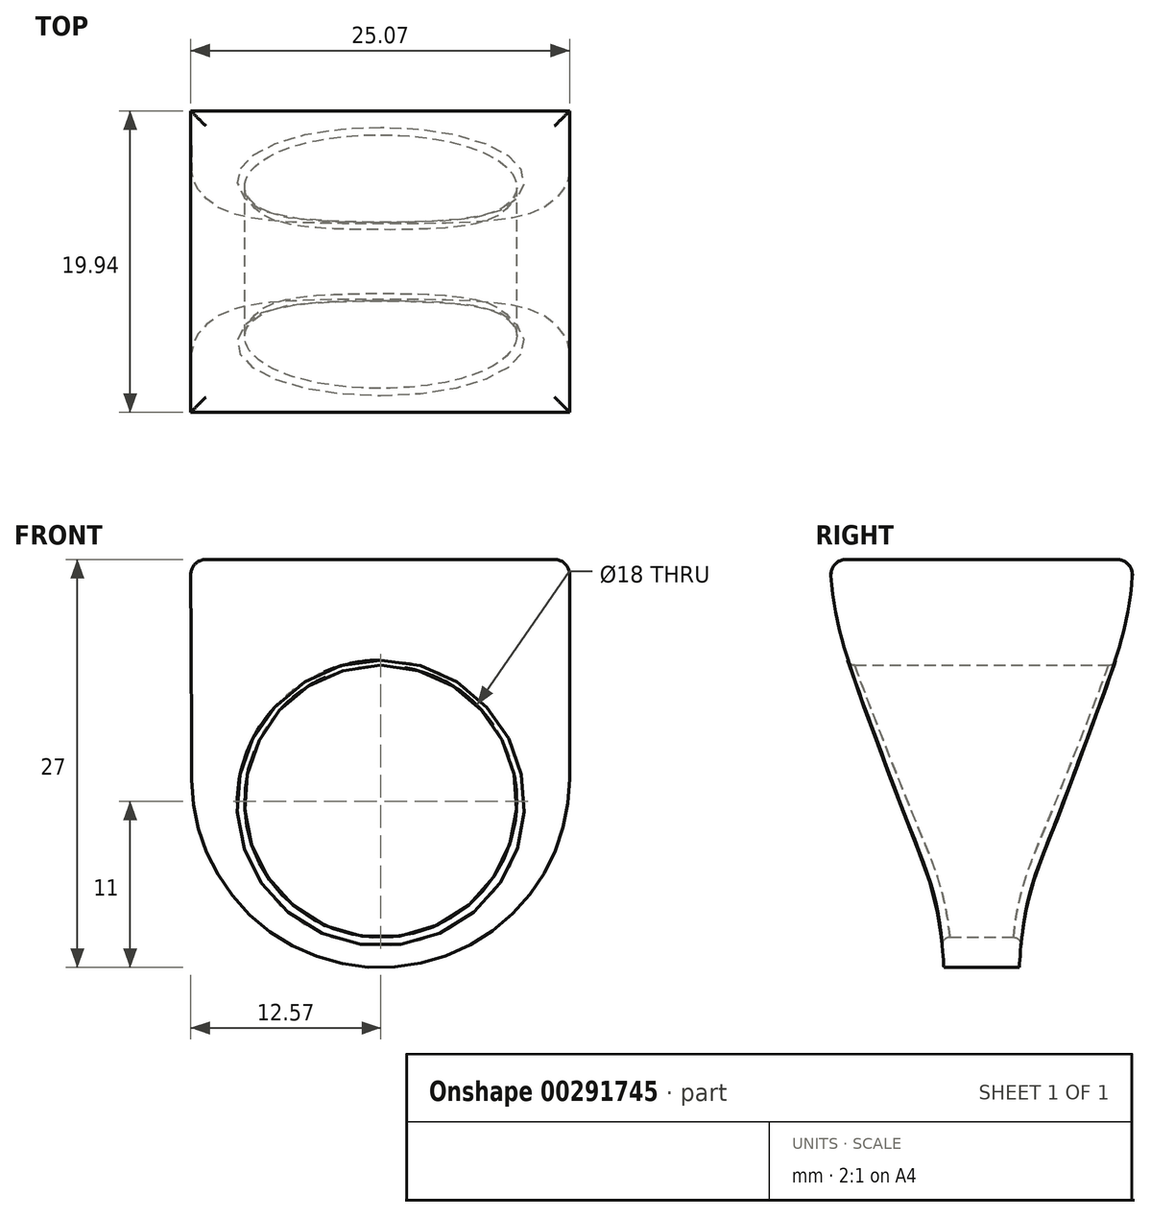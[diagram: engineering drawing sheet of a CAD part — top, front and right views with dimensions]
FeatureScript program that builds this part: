
annotation { "Feature Type Name" : "Feature", "Feature Type Description" : "" }
export const myFeature = defineFeature(function(context is Context, id is Id, definition is map)
    precondition{}
    {
        {
            assignVariable(context, id + "F0", {"name" : "ring_brete", "anyValue" : 20 * mm});
        }
        {
            var Q0;
            Q0=qCreatedBy(makeId("Front.planeOp"),FACE);
            var sketch = newSketch(context, id + "F1", { "sketchPlane" : qUnion([Q0])});
            skCircle(sketch, "E0", {"center": v(0, 0) * mm, "radius": 9 * mm});
            skCircle(sketch, "E1", {"center": v(0, 1.5) * mm, "radius": 12.5 * mm});
            skLineSegment(sketch, "E2", {"start": v(-12.5, 1.43) * mm, "end": v(-12.58, 16) * mm});
            skLineSegment(sketch, "E3", {"start": v(-12.58, 16) * mm, "end": v(12.5, 16) * mm});
            skLineSegment(sketch, "E4", {"start": v(12.5, 16) * mm, "end": v(12.5, 1.5) * mm});
            skSolve(sketch);
        }
        {
            var Q0;
            {var subQ0=sQuery(id+"F1.wireOp",EDGE,"E2");Q0=makeQuery(id+"F1.imprint","IMPRINT",FACE,{"disambiguationData":[TD([[makeQuery(id+"F1.imprint","IMPRINT",EDGE,{"derivedFrom":subQ0}),-1.0]])]});}
            var Q1;
            Q1=makeQuery(id+"F1.imprint","IMPRINT",FACE,{"disambiguationData":[TD([[makeQuery(id+"F1.imprint","IMPRINT",EDGE,{"derivedFrom":sQuery(id+"F1.wireOp",EDGE,"E0")}),-1.0]])]});
            extrude(context, id + "F2", {"entities" : qUnion([Q0, Q1]), "depth" : getVariable(context, 'ring_brete'), "offsetDistance" : 25 * mm, "symmetric" : true});
        }
        {
            var Q0;
            Q0=makeQuery(id+"F2.opExtrude","SWEPT_FACE",FACE,{"disambiguationData":[OSD([sQuery(id+"F1.wireOp",EDGE,"E2")])]});
            var sketch = newSketch(context, id + "F3", { "sketchPlane" : qUnion([Q0])});
            skLineSegment(sketch, "E5.0", {"start": v(10, 16.07) * mm, "end": v(-10, 16.07) * mm, "construction": true});
            skLineSegment(sketch, "E6", {"start": v(10, -11) * mm, "end": v(-10, -11) * mm, "construction": true});
            skLineSegment(sketch, "E7.0", {"start": v(10, 1.5) * mm, "end": v(10, 16.07) * mm, "construction": true});
            skFitSpline(sketch, "E8", {"points": [v(10, 16.07) * mm, v(8, 6.88) * mm, v(4.5, -2.44) * mm, v(2.5, -11) * mm], "startDerivative": vector(0, -32.36) * mm, "endDerivative": vector(-1.97, -39.16) * mm});
            skLineSegment(sketch, "E9", {"start": v(2.5, -11) * mm, "end": v(20, -11) * mm});
            skLineSegment(sketch, "E10", {"start": v(20, -11) * mm, "end": v(20, 16.07) * mm});
            skLineSegment(sketch, "E11", {"start": v(20, 16.07) * mm, "end": v(10, 16.07) * mm});
            skLineSegment(sketch, "E12", {"start": v(0, 0) * mm, "end": v(0, 12.28) * mm, "construction": true});
            skLineSegment(sketch, "E13.MirrorCS", {"start": v(-20, 16.07) * mm, "end": v(-10, 16.07) * mm});
            skLineSegment(sketch, "E14.MirrorCS", {"start": v(-10, 16.07) * mm, "end": v(10, 16.07) * mm, "construction": true});
            skLineSegment(sketch, "E15.MirrorCS", {"start": v(-10, 1.5) * mm, "end": v(-10, 16.07) * mm, "construction": true});
            skLineSegment(sketch, "E16.MirrorCS", {"start": v(-20, -11) * mm, "end": v(-20, 16.07) * mm});
            skLineSegment(sketch, "E17.MirrorCS", {"start": v(-2.5, -11) * mm, "end": v(-20, -11) * mm});
            skLineSegment(sketch, "E18.MirrorCS", {"start": v(-10, -11) * mm, "end": v(10, -11) * mm, "construction": true});
            skFitSpline(sketch, "E19.MirrorCS", {"points": [v(-10, 16.07) * mm, v(-8, 6.88) * mm, v(-4.5, -2.44) * mm, v(-2.5, -11) * mm], "startDerivative": vector(0, -32.36) * mm, "endDerivative": vector(1.97, -39.16) * mm});
            skSolve(sketch);
        }
        {
            var Q0;
            Q0 = qSketchRegion(id + "F3", true);
            extrude(context, id + "F4", {"entities" : qUnion([Q0]), "operationType" : NewBodyOperationType.REMOVE, "endBound" : BoundingType.THROUGH_ALL, "oppositeDirection" : true, "depth" : 25 * mm, "offsetDistance" : 25 * mm});
        }
        {
            var Q0;
            Q0=makeQuery(id+"F4.boolean.opBoolean","INTERSECT",EDGE,{"derivedFrom":[makeQuery(id+"F2.opExtrude","SWEPT_FACE",FACE,{"disambiguationData":[OSD([sQuery(id+"F1.wireOp",EDGE,"E0")])]}),makeQuery(id+"F4.opExtrude","SWEPT_FACE",FACE,{"disambiguationData":[OSD([sQuery(id+"F3.wireOp",EDGE,"E19.MirrorCS")])]})]});
            var Q1;
            Q1=makeQuery(id+"F4.boolean.opBoolean","INTERSECT",EDGE,{"derivedFrom":[makeQuery(id+"F2.opExtrude","SWEPT_FACE",FACE,{"disambiguationData":[OSD([sQuery(id+"F1.wireOp",EDGE,"E0")])]}),makeQuery(id+"F4.opExtrude","SWEPT_FACE",FACE,{"disambiguationData":[OSD([sQuery(id+"F3.wireOp",EDGE,"E8")])]})]});
            fillet(context, id + "F5", {"entities" : qUnion([Q0, Q1]), "radius" : 0.5 * mm, "tangentPropagation" : true, "allowEdgeOverflow" : false});
        }
        {
            var Q0;
            Q0=makeQuery(id+"F4.boolean.opBoolean","COPY",EDGE,{"derivedFrom":makeQuery(id+"F4.opExtrude","CAP_EDGE",EDGE,{"disambiguationData":[OSD([sQuery(id+"F3.wireOp",EDGE,"E8")])],"isStart":true})});
            var Q1;
            Q1=makeQuery(id+"F4.boolean.opBoolean","COPY",EDGE,{"derivedFrom":makeQuery(id+"F4.opExtrude","CAP_EDGE",EDGE,{"disambiguationData":[OSD([sQuery(id+"F3.wireOp",EDGE,"E19.MirrorCS")])],"isStart":true})});
            var Q2;
            Q2=makeQuery(id+"F2.opExtrude","SWEPT_FACE",FACE,{"disambiguationData":[OSD([sQuery(id+"F1.wireOp",EDGE,"E3")])]});
            fillet(context, id + "F6", {"entities" : qUnion([Q0, Q1, Q2]), "radius" : 1 * mm, "tangentPropagation" : true, "allowEdgeOverflow" : false});
        }
    });
